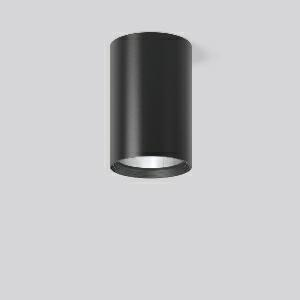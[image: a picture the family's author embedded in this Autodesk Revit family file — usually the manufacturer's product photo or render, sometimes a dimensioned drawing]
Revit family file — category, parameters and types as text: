
# Revit family: heledon_maxi_a_931226_003_2_76_7974
name_source: partatom
category: Lighting Fixtures
units: mm (PartAtom-declared; Revit-internal decimal feet)

## family parameters
Cut with Voids When Loaded = No
Host = Face
Light Source = No
Part Type = Normal
Room Calculation Point = No
Round Connector Dimension = Use Diameter
Shared = No

## types (1)
- HELEDON maxi A (1 x LED Modul 927, 3950 lm, 2700)
    Apparent Load = 35 VA
    Approval mark = CE
    CIE Flux Codes = 97 100 100 100 100
    Color Rendering = 92
    Color Temperature = 2700
    Default Elevation = 1800 mm
    Description = Series: HELEDON maxi
Cylindrical surface-mounted downlight. Housing: die-cast aluminium, powder-coated. Internal ceiling frame polycarbonate with bayonet mounting. Black plastic ring and recessed LED to prevent glare from the side. Optical assembly with reflector made of MIRO-Silver with 98% total light reflection for outstanding efficiency - can be changed without tools. Best colour rendering index Ra>90. Suitable for Ceiling mounting. Easy installation with a separate ceiling frame with bayonet mounting and plug connection. Driver integrated. Connected via plug-in connector. High quality converter without flickering and stroboscopic effect. The following accessories can be mounted without use of tools: interchangeable lenses, decorative glasses, honeycomb louvre, clear and frosted diffusers, white interchangeable plastic ring. 
Colour: deep black, matt (RAL 9005)
Diameter: 123 mm
Height: 183 mm
Lamp: LED
Socket: without socket
Colour temperature: 2700K
Colour rendering index (CRI): 92
System power: 35 W
Rated luminous flux: 3950 lm
Luminous efficiency: 113 lm/W
Control gear: Converter, dimmable, DALI
Protection class: I
Type of protection: IP 20
    Height = 183 mm
    Lamp = 1 x LED Modul 927
    Lamp Light Flux = 3950 lm
    Lamp count = 1
    Length = 123 mm
    Lifetime = 50000 h
    Luminous efficacy = 113 lm/W
    Manufacturer = RZB
    ModVariant = No
    Model = 931226.003.2.76
    Mounting Place = Ceiling
    Mounting Type = Surface mounted
    Number of Poles = 1
    OnlyDefault = Yes
    Power Factor = 1
    Product Name = HELEDON maxi A
    Product group = Surface mounted downlights
    ProductGroupID = 302
    Protection Class = Protection class I
    Protection Degree = IP 20
    RLX_Detail_Level = 1
    RLX_Emergency_Light_Flux = 0 lm
    RLX_Emergency_Type = 0
    RLX_Emergency_Type_DB = No
    RlxData = <blob elided: 98573 chars, md5=458f2078>
    Socket = socket
    Standby Power = 0 W
    System Light Flux = 3950 lm
    System Power = 35 W
    Type Comments = Product without accessories
    Type Image = 931192.003.jpg
    URL = http://relux.com
    VarID = ---
    Voltage = 230 V
    Voltage Range = 220-240 V
    Weight = 0.00 kg
    Width = 0 mm  [stored 0 ft]

note: [stored X ft] marks values corroborated as IEEE doubles in the binary element streams (Revit-internal decimal feet)

## geometry (parser evidence)
native form markers: Blend x4, Sweep x10
no freeform markers — native parametric forms only
